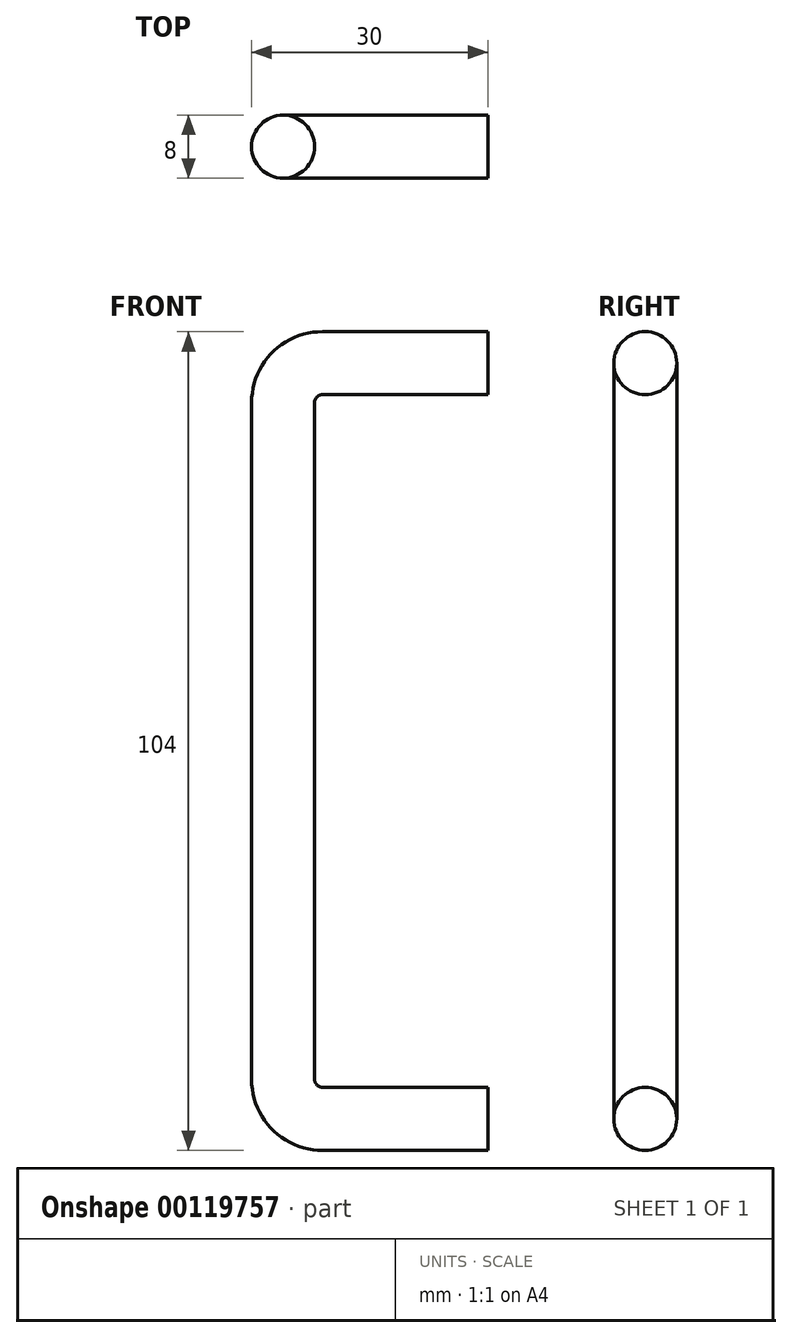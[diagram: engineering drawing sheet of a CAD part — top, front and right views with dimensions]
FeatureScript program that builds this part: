
annotation { "Feature Type Name" : "Feature", "Feature Type Description" : "" }
export const myFeature = defineFeature(function(context is Context, id is Id, definition is map)
    precondition{}
    {
        {
            var Q0;
            Q0=qCreatedBy(makeId("Front.planeOp"),FACE);
            var sketch = newSketch(context, id + "F0", { "sketchPlane" : qUnion([Q0])});
            skLineSegment(sketch, "E0", {"start": v(0, 0) * mm, "end": v(-21, 0) * mm});
            skLineSegment(sketch, "E1", {"start": v(-26, 5) * mm, "end": v(-26, 91) * mm});
            skLineSegment(sketch, "E2", {"start": v(-21, 96) * mm, "end": v(0, 96) * mm});
            skPoint(sketch, "E3.visualSharp", {"position": v(-26, 96) * mm});
            skArc(sketch, "E3.filletArc", {"start": v(-21, 96) * mm, "mid": v(-24.54, 94.54) * mm, "end": v(-26, 91) * mm});
            skPoint(sketch, "E4.visualSharp", {"position": v(-26, 0) * mm});
            skArc(sketch, "E4.filletArc", {"start": v(-26, 5) * mm, "mid": v(-24.54, 1.46) * mm, "end": v(-21, 0) * mm});
            skSolve(sketch);
        }
        {
            var Q0;
            Q0=qCreatedBy(makeId("Right.planeOp"),FACE);
            var sketch = newSketch(context, id + "F1", { "sketchPlane" : qUnion([Q0])});
            skCircle(sketch, "E5", {"center": v(0, 0) * mm, "radius": 4 * mm});
            skSolve(sketch);
        }
        {
            var Q0;
            Q0=makeQuery(id+"F1.imprint","IMPRINT",FACE,{"disambiguationData":[TD([[makeQuery(id+"F1.imprint","IMPRINT",EDGE,{"derivedFrom":sQuery(id+"F1.wireOp",EDGE,"E5")}),1.0]])]});
            var Q1;
            Q1=sQuery(id+"F0.wireOp",EDGE,"E0");
            var Q2;
            Q2=sQuery(id+"F0.wireOp",EDGE,"E4.filletArc");
            var Q3;
            Q3=sQuery(id+"F0.wireOp",EDGE,"E1");
            var Q4;
            Q4=sQuery(id+"F0.wireOp",EDGE,"E3.filletArc");
            var Q5;
            Q5=sQuery(id+"F0.wireOp",EDGE,"E2");
            sweep(context, id + "F2", {"profiles" : qUnion([Q0]), "path" : qUnion([Q1, Q2, Q3, Q4, Q5])});
        }
    });
